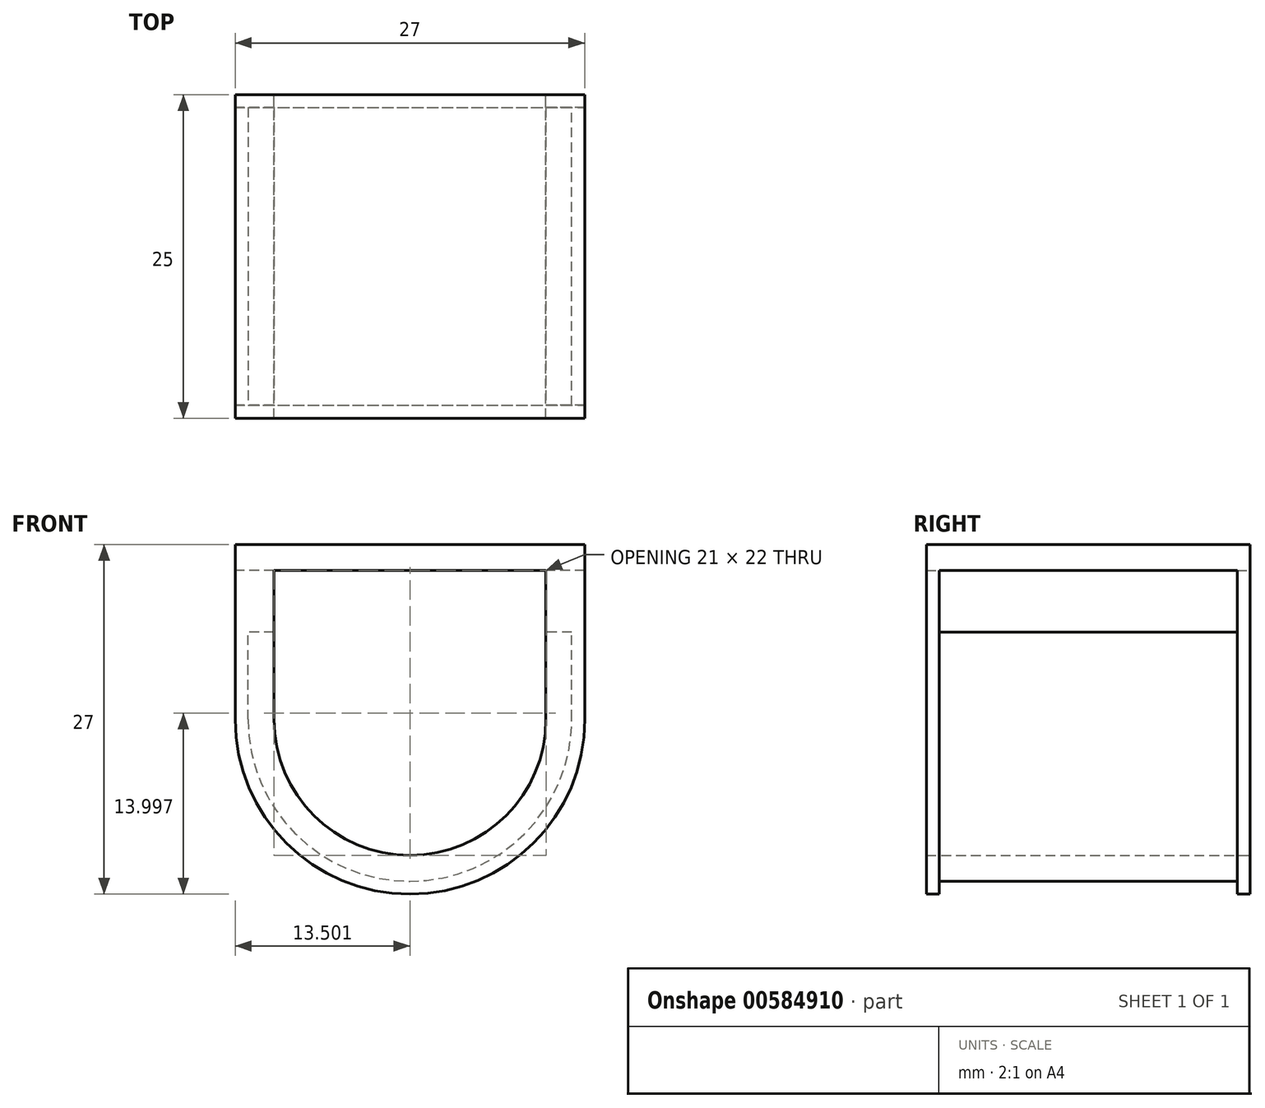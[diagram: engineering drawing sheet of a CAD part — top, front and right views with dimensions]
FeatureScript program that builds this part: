
annotation { "Feature Type Name" : "Feature", "Feature Type Description" : "" }
export const myFeature = defineFeature(function(context is Context, id is Id, definition is map)
    precondition{}
    {
        {
            var Q0;
            Q0=qCreatedBy(makeId("Front.planeOp"),FACE);
            var sketch = newSketch(context, id + "F0", { "sketchPlane" : qUnion([Q0])});
            skPoint(sketch, "E0", {"position": v(-1.93, -50.17) * mm});
            skLineSegment(sketch, "E1.bottom", {"start": v(-15.43, 15.52) * mm, "end": v(11.57, 15.52) * mm});
            skLineSegment(sketch, "E1.top", {"start": v(-15.43, -11.48) * mm, "end": v(11.57, -11.48) * mm});
            skLineSegment(sketch, "E1.left", {"start": v(-15.43, 15.52) * mm, "end": v(-15.43, -11.48) * mm});
            skLineSegment(sketch, "E1.right", {"start": v(11.57, 15.52) * mm, "end": v(11.57, -11.48) * mm});
            skPoint(sketch, "E2", {"position": v(-1.93, 15.52) * mm});
            skPoint(sketch, "E3.positionSnap0", {"position": v(11.57, 2.02) * mm});
            skArc(sketch, "E4", {"start": v(-15.43, 2.02) * mm, "mid": v(-1.93, -11.48) * mm, "end": v(11.57, 2.02) * mm});
            skPoint(sketch, "E5", {"position": v(11.57, 15.52) * mm});
            skPoint(sketch, "E6", {"position": v(-14.43, 2.02) * mm});
            skPoint(sketch, "E7", {"position": v(10.57, 2.02) * mm});
            skArc(sketch, "E8", {"start": v(-14.43, 2.02) * mm, "mid": v(-1.93, -10.48) * mm, "end": v(10.57, 2.02) * mm});
            skLineSegment(sketch, "E9", {"start": v(-14.43, 2.02) * mm, "end": v(-14.43, 15.52) * mm});
            skLineSegment(sketch, "E10", {"start": v(10.57, 2.02) * mm, "end": v(10.57, 15.52) * mm});
            skPoint(sketch, "E11", {"position": v(8.57, 2.02) * mm});
            skPoint(sketch, "E12", {"position": v(-12.43, 2.02) * mm});
            skArc(sketch, "E13", {"start": v(8.57, 2.02) * mm, "mid": v(-1.93, -8.48) * mm, "end": v(-12.43, 2.02) * mm});
            skLineSegment(sketch, "E14", {"start": v(8.57, 2.02) * mm, "end": v(8.57, 15.52) * mm});
            skLineSegment(sketch, "E15", {"start": v(-12.43, 2.02) * mm, "end": v(-12.43, 15.52) * mm});
            skPoint(sketch, "E16", {"position": v(11.57, 13.52) * mm});
            skLineSegment(sketch, "E17", {"start": v(11.57, 13.52) * mm, "end": v(-15.43, 13.52) * mm});
            skSolve(sketch);
        }
        {
            var Q0;
            Q0=makeQuery(id+"F0.imprint","IMPRINT",FACE,{"disambiguationData":[TD([[makeQuery(id+"F0.imprint","IMPRINT",EDGE,{"derivedFrom":sQuery(id+"F0.wireOp",EDGE,"E8")}),1.0]])]});
            var Q1;
            {var subQ0=sQuery(id+"F0.wireOp",EDGE,"E10");var subQ1=sQuery(id+"F0.wireOp",EDGE,"E1.bottom");var subQ2=makeQuery(id+"F0.imprint","INTERSECT",VERTEX,{"derivedFrom":[subQ1,subQ0]});Q1=makeQuery(id+"F0.imprint","IMPRINT",FACE,{"disambiguationData":[TD([[makeQuery(id+"F0.imprint","IMPRINT",EDGE,{"disambiguationData":[TD([[subQ2,1.0]])],"derivedFrom":subQ1}),-1.0]])]});}
            var Q2;
            {var subQ0=sQuery(id+"F0.wireOp",EDGE,"E9");var subQ1=sQuery(id+"F0.wireOp",EDGE,"E1.bottom");var subQ2=makeQuery(id+"F0.imprint","INTERSECT",VERTEX,{"derivedFrom":[subQ1,subQ0]});Q2=makeQuery(id+"F0.imprint","IMPRINT",FACE,{"disambiguationData":[TD([[makeQuery(id+"F0.imprint","IMPRINT",EDGE,{"disambiguationData":[TD([[subQ2,-1.0]])],"derivedFrom":subQ1}),-1.0]])]});}
            var Q3;
            {var subQ0=sQuery(id+"F0.wireOp",EDGE,"E1.left");var subQ1=sQuery(id+"F0.wireOp",EDGE,"E1.bottom");var subQ2=makeQuery(id+"F0.imprint","INTERSECT",VERTEX,{"derivedFrom":[subQ1,subQ0]});Q3=makeQuery(id+"F0.imprint","IMPRINT",FACE,{"disambiguationData":[TD([[makeQuery(id+"F0.imprint","IMPRINT",EDGE,{"disambiguationData":[TD([[subQ2,-1.0]])],"derivedFrom":subQ1}),-1.0]])]});}
            var Q4;
            {var subQ0=sQuery(id+"F0.wireOp",EDGE,"E14");var subQ1=sQuery(id+"F0.wireOp",EDGE,"E1.bottom");var subQ2=makeQuery(id+"F0.imprint","INTERSECT",VERTEX,{"derivedFrom":[subQ1,subQ0]});Q4=makeQuery(id+"F0.imprint","IMPRINT",FACE,{"disambiguationData":[TD([[makeQuery(id+"F0.imprint","IMPRINT",EDGE,{"disambiguationData":[TD([[subQ2,1.0]])],"derivedFrom":subQ1}),-1.0]])]});}
            var Q5;
            {var subQ0=sQuery(id+"F0.wireOp",EDGE,"E1.right");var subQ1=sQuery(id+"F0.wireOp",EDGE,"E1.bottom");var subQ2=makeQuery(id+"F0.imprint","INTERSECT",VERTEX,{"derivedFrom":[subQ1,subQ0]});Q5=makeQuery(id+"F0.imprint","IMPRINT",FACE,{"disambiguationData":[TD([[makeQuery(id+"F0.imprint","IMPRINT",EDGE,{"disambiguationData":[TD([[subQ2,1.0]])],"derivedFrom":subQ1}),-1.0]])]});}
            extrude(context, id + "F1", {"entities" : qUnion([Q0, Q1, Q2, Q3, Q4, Q5]), "depth" : 25 * mm, "offsetDistance" : 25 * mm});
        }
        {
            var Q0;
            Q0=makeQuery(id+"F0.imprint","IMPRINT",FACE,{"disambiguationData":[TD([[makeQuery(id+"F0.imprint","IMPRINT",EDGE,{"derivedFrom":sQuery(id+"F0.wireOp",EDGE,"E8")}),-1.0]])]});
            var Q1;
            Q1=makeQuery(id+"F0.imprint","IMPRINT",FACE,{"disambiguationData":[TD([[makeQuery(id+"F0.imprint","IMPRINT",EDGE,{"derivedFrom":sQuery(id+"F0.wireOp",EDGE,"E8")}),1.0]])]});
            var Q2;
            Q2=makeQuery(id+"F0.imprint","IMPRINT",FACE,{"disambiguationData":[TD([[makeQuery(id+"F0.imprint","IMPRINT",EDGE,{"derivedFrom":sQuery(id+"F0.wireOp",EDGE,"E13")}),-1.0]])]});
            extrude(context, id + "F2", {"entities" : qUnion([Q0, Q1, Q2]), "operationType" : NewBodyOperationType.ADD, "depth" : 1 * mm, "offsetDistance" : 25 * mm});
        }
        {
            var Q0;
            Q0=makeQuery(id+"F0.imprint","IMPRINT",FACE,{"disambiguationData":[TD([[makeQuery(id+"F0.imprint","IMPRINT",EDGE,{"derivedFrom":sQuery(id+"F0.wireOp",EDGE,"E8")}),-1.0]])]});
            var Q1;
            Q1=makeQuery(id+"F0.imprint","IMPRINT",FACE,{"disambiguationData":[TD([[makeQuery(id+"F0.imprint","IMPRINT",EDGE,{"derivedFrom":sQuery(id+"F0.wireOp",EDGE,"E8")}),1.0]])]});
            var Q2;
            Q2=makeQuery(id+"F0.imprint","IMPRINT",FACE,{"disambiguationData":[TD([[makeQuery(id+"F0.imprint","IMPRINT",EDGE,{"derivedFrom":sQuery(id+"F0.wireOp",EDGE,"E13")}),-1.0]])]});
            extrude(context, id + "F3", {"entities" : qUnion([Q0, Q1, Q2]), "operationType" : NewBodyOperationType.ADD, "depth" : 25 * mm, "offsetDistance" : 25 * mm, "hasSecondDirection" : true, "secondDirectionOppositeDirection" : false, "secondDirectionDepth" : 24 * mm});
        }
        {
            var Q0;
            Q0=makeQuery(id+"F1.opExtrude","SWEPT_FACE",FACE,{"disambiguationData":[OSD([sQuery(id+"F0.wireOp",EDGE,"E9")])]});
            var sketch = newSketch(context, id + "F4", { "sketchPlane" : qUnion([Q0])});
            skLineSegment(sketch, "E18.bottom", {"start": v(1, 15.52) * mm, "end": v(24, 15.52) * mm});
            skLineSegment(sketch, "E18.top", {"start": v(1, 8.77) * mm, "end": v(24, 8.77) * mm});
            skLineSegment(sketch, "E18.left", {"start": v(1, 15.52) * mm, "end": v(1, 8.77) * mm});
            skLineSegment(sketch, "E18.right", {"start": v(24, 15.52) * mm, "end": v(24, 8.77) * mm});
            skPoint(sketch, "E19", {"position": v(1, 13.52) * mm});
            skLineSegment(sketch, "E20", {"start": v(1, 13.52) * mm, "end": v(24, 13.52) * mm});
            skSolve(sketch);
        }
        {
            var Q0;
            {var subQ0=sQuery(id+"F4.wireOp",EDGE,"E18.top");Q0=makeQuery(id+"F4.imprint","IMPRINT",FACE,{"disambiguationData":[TD([[makeQuery(id+"F4.imprint","IMPRINT",EDGE,{"derivedFrom":subQ0}),1.0]])]});}
            var Q1;
            Q1=makeQuery(id+"F1.opExtrude","SWEPT_FACE",FACE,{"disambiguationData":[OSD([sQuery(id+"F0.wireOp",EDGE,"E10")])]});
            extrude(context, id + "F5", {"entities" : qUnion([Q0]), "operationType" : NewBodyOperationType.REMOVE, "endBound" : BoundingType.UP_TO_SURFACE, "oppositeDirection" : true, "depth" : 25 * mm, "endBoundEntityFace" : qUnion([Q1]), "offsetDistance" : 25 * mm});
        }
    });
